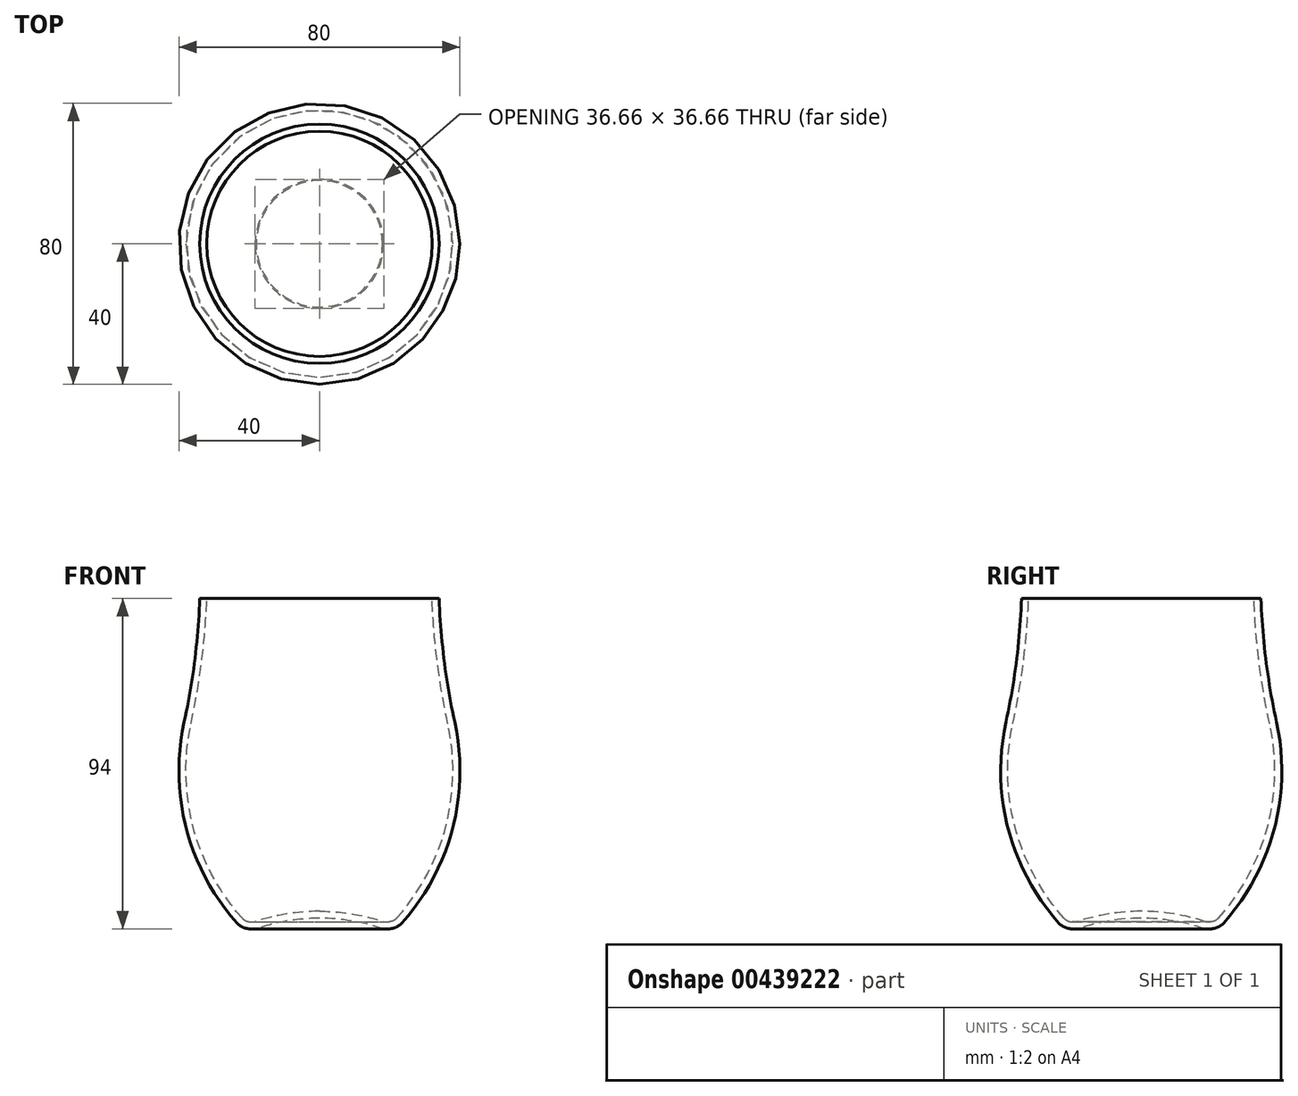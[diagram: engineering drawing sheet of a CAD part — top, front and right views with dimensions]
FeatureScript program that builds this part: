
annotation { "Feature Type Name" : "Feature", "Feature Type Description" : "" }
export const myFeature = defineFeature(function(context is Context, id is Id, definition is map)
    precondition{}
    {
        {
            var Q0;
            Q0=qCreatedBy(makeId("Front.planeOp"),FACE);
            var sketch = newSketch(context, id + "F0", { "sketchPlane" : qUnion([Q0])});
            skLineSegment(sketch, "E0", {"start": v(-18.56, -28.5) * mm, "end": v(-3.7, -28.5) * mm});
            skArc(sketch, "E1", {"start": v(-31.05, -3.22) * mm, "mid": v(-28.63, -15.59) * mm, "end": v(-22.48, -26.6) * mm});
            skLineSegment(sketch, "E2", {"start": v(-31.05, -3.22) * mm, "end": v(-33.2, 58.5) * mm});
            skLineSegment(sketch, "E3", {"start": v(-1.98, -33.5) * mm, "end": v(-2.72, -29.32) * mm});
            skArc(sketch, "E4", {"start": v(-2.72, -29.32) * mm, "mid": v(-3.06, -28.73) * mm, "end": v(-3.7, -28.5) * mm});
            skArc(sketch, "E5", {"start": v(-22.48, -26.6) * mm, "mid": v(-20.74, -28) * mm, "end": v(-18.56, -28.5) * mm});
            skLineSegment(sketch, "E6", {"start": v(0.02, -33.5) * mm, "end": v(-1.98, -33.5) * mm});
            skLineSegment(sketch, "E7", {"start": v(-32.04, 60) * mm, "end": v(-32.68, 60) * mm});
            skLineSegment(sketch, "E8", {"start": v(-32.04, 60) * mm, "end": v(0, 60) * mm});
            skArc(sketch, "E9", {"start": v(-33.15, 58.66) * mm, "mid": v(-33.18, 58.58) * mm, "end": v(-33.2, 58.5) * mm});
            skArc(sketch, "E10", {"start": v(-32.68, 60) * mm, "mid": v(-33.39, 59.5) * mm, "end": v(-33.15, 58.66) * mm});
            skArc(sketch, "E11", {"start": v(-21.95, -21.82) * mm, "mid": v(-20.14, -23.5) * mm, "end": v(-17.75, -24.1) * mm});
            skArc(sketch, "E12", {"start": v(-30.8, 59.43) * mm, "mid": v(-30.98, 59.84) * mm, "end": v(-31.4, 60) * mm});
            skLineSegment(sketch, "E13", {"start": v(-32.04, 60) * mm, "end": v(-31.4, 60) * mm});
            skLineSegment(sketch, "E14", {"start": v(-27.82, -3.55) * mm, "end": v(-30.8, 59.43) * mm});
            skArc(sketch, "E15", {"start": v(-27.82, -3.55) * mm, "mid": v(-26.1, -13.07) * mm, "end": v(-21.95, -21.82) * mm});
            skArc(sketch, "E16", {"start": v(-3.12, -47.12) * mm, "mid": v(-1.62, -47.77) * mm, "end": v(0, -48) * mm});
            skArc(sketch, "E17", {"start": v(-3.12, -47.12) * mm, "mid": v(-9.17, -48.1) * mm, "end": v(-15, -50) * mm});
            skArc(sketch, "E18", {"start": v(0, -45) * mm, "mid": v(-7.84, -45.75) * mm, "end": v(-15.4, -48) * mm});
            skArc(sketch, "E19", {"start": v(-33.63, 59.25) * mm, "mid": v(-33.5, 58.86) * mm, "end": v(-33.13, 58.66) * mm});
            skArc(sketch, "E20", {"start": v(-32.88, 60) * mm, "mid": v(-33.41, 59.78) * mm, "end": v(-33.63, 59.25) * mm});
            skArc(sketch, "E21", {"start": v(-34, 36.18) * mm, "mid": v(-33.25, 47.4) * mm, "end": v(-33.13, 58.66) * mm});
            skLineSegment(sketch, "E22", {"start": v(-21.19, -50) * mm, "end": v(0, -50) * mm});
            skArc(sketch, "E23", {"start": v(-40.33, 5.1) * mm, "mid": v(-40.55, -24.39) * mm, "end": v(-24.12, -48.89) * mm});
            skArc(sketch, "E24", {"start": v(-24.12, -48.89) * mm, "mid": v(-22.64, -49.72) * mm, "end": v(-20.97, -50) * mm});
            skArc(sketch, "E25", {"start": v(-40.33, 5.1) * mm, "mid": v(-36.34, 20.47) * mm, "end": v(-34, 36.18) * mm});
            skArc(sketch, "E26", {"start": v(-32.01, 35.99) * mm, "mid": v(-31.24, 47.69) * mm, "end": v(-31.15, 59.41) * mm});
            skArc(sketch, "E27", {"start": v(-38.42, 4.5) * mm, "mid": v(-34.38, 20.08) * mm, "end": v(-32.01, 35.99) * mm});
            skArc(sketch, "E28", {"start": v(-38.42, 4.5) * mm, "mid": v(-38.64, -23.81) * mm, "end": v(-22.86, -47.33) * mm});
            skArc(sketch, "E29", {"start": v(-22.86, -47.33) * mm, "mid": v(-21.98, -47.83) * mm, "end": v(-20.97, -48) * mm});
            skLineSegment(sketch, "E30", {"start": v(-21.14, -48) * mm, "end": v(-15.4, -48) * mm});
            skArc(sketch, "E31", {"start": v(-31.15, 59.41) * mm, "mid": v(-31.33, 59.83) * mm, "end": v(-31.75, 60) * mm});
            skLineSegment(sketch, "E32", {"start": v(-32.88, 60) * mm, "end": v(-31.75, 60) * mm});
            skLineSegment(sketch, "E33", {"start": v(-28.41, 60) * mm, "end": v(0, 60) * mm});
            skLineSegment(sketch, "E34", {"start": v(-17.75, -24.1) * mm, "end": v(0, -24.1) * mm});
            skLineSegment(sketch, "E35", {"start": v(18.56, -28.5) * mm, "end": v(3.7, -28.5) * mm});
            skArc(sketch, "E36", {"start": v(22.48, -26.6) * mm, "mid": v(28.63, -15.59) * mm, "end": v(31.05, -3.22) * mm});
            skLineSegment(sketch, "E37", {"start": v(31.05, -3.22) * mm, "end": v(33.2, 58.5) * mm});
            skLineSegment(sketch, "E38", {"start": v(1.98, -33.5) * mm, "end": v(2.72, -29.32) * mm});
            skArc(sketch, "E39", {"start": v(3.7, -28.5) * mm, "mid": v(3.06, -28.73) * mm, "end": v(2.72, -29.32) * mm});
            skArc(sketch, "E40", {"start": v(18.56, -28.5) * mm, "mid": v(20.74, -28) * mm, "end": v(22.48, -26.6) * mm});
            skLineSegment(sketch, "E41", {"start": v(-0.02, -33.5) * mm, "end": v(1.98, -33.5) * mm});
            skLineSegment(sketch, "E42", {"start": v(32.04, 60) * mm, "end": v(32.68, 60) * mm});
            skLineSegment(sketch, "E43", {"start": v(32.04, 60) * mm, "end": v(0, 60) * mm});
            skArc(sketch, "E44", {"start": v(33.2, 58.5) * mm, "mid": v(33.18, 58.58) * mm, "end": v(33.15, 58.66) * mm});
            skArc(sketch, "E45", {"start": v(33.15, 58.66) * mm, "mid": v(33.39, 59.5) * mm, "end": v(32.68, 60) * mm});
            skArc(sketch, "E46", {"start": v(17.75, -24.1) * mm, "mid": v(20.14, -23.5) * mm, "end": v(21.95, -21.82) * mm});
            skArc(sketch, "E47", {"start": v(31.4, 60) * mm, "mid": v(30.98, 59.84) * mm, "end": v(30.8, 59.43) * mm});
            skLineSegment(sketch, "E48", {"start": v(32.04, 60) * mm, "end": v(31.4, 60) * mm});
            skLineSegment(sketch, "E49", {"start": v(27.82, -3.55) * mm, "end": v(30.8, 59.43) * mm});
            skArc(sketch, "E50", {"start": v(21.95, -21.82) * mm, "mid": v(26.1, -13.07) * mm, "end": v(27.82, -3.55) * mm});
            skArc(sketch, "E51", {"start": v(0, -48) * mm, "mid": v(1.62, -47.77) * mm, "end": v(3.12, -47.12) * mm});
            skArc(sketch, "E52", {"start": v(15, -50) * mm, "mid": v(9.17, -48.1) * mm, "end": v(3.12, -47.12) * mm});
            skArc(sketch, "E53", {"start": v(15.4, -48) * mm, "mid": v(7.84, -45.75) * mm, "end": v(0, -45) * mm});
            skArc(sketch, "E54", {"start": v(33.13, 58.66) * mm, "mid": v(33.5, 58.86) * mm, "end": v(33.63, 59.25) * mm});
            skArc(sketch, "E55", {"start": v(33.63, 59.25) * mm, "mid": v(33.41, 59.78) * mm, "end": v(32.88, 60) * mm});
            skArc(sketch, "E56", {"start": v(33.13, 58.66) * mm, "mid": v(33.25, 47.4) * mm, "end": v(34, 36.18) * mm});
            skLineSegment(sketch, "E57", {"start": v(21.19, -50) * mm, "end": v(0, -50) * mm});
            skArc(sketch, "E58", {"start": v(24.12, -48.89) * mm, "mid": v(40.55, -24.39) * mm, "end": v(40.33, 5.1) * mm});
            skArc(sketch, "E59", {"start": v(20.97, -50) * mm, "mid": v(22.64, -49.72) * mm, "end": v(24.12, -48.89) * mm});
            skArc(sketch, "E60", {"start": v(34, 36.18) * mm, "mid": v(36.34, 20.47) * mm, "end": v(40.33, 5.1) * mm});
            skArc(sketch, "E61", {"start": v(31.15, 59.41) * mm, "mid": v(31.24, 47.69) * mm, "end": v(32.01, 35.99) * mm});
            skArc(sketch, "E62", {"start": v(32.01, 35.99) * mm, "mid": v(34.38, 20.08) * mm, "end": v(38.42, 4.5) * mm});
            skArc(sketch, "E63", {"start": v(22.86, -47.33) * mm, "mid": v(38.64, -23.81) * mm, "end": v(38.42, 4.5) * mm});
            skArc(sketch, "E64", {"start": v(20.97, -48) * mm, "mid": v(21.98, -47.83) * mm, "end": v(22.86, -47.33) * mm});
            skLineSegment(sketch, "E65", {"start": v(21.14, -48) * mm, "end": v(15.4, -48) * mm});
            skArc(sketch, "E66", {"start": v(31.75, 60) * mm, "mid": v(31.33, 59.83) * mm, "end": v(31.15, 59.41) * mm});
            skLineSegment(sketch, "E67", {"start": v(32.88, 60) * mm, "end": v(31.75, 60) * mm});
            skLineSegment(sketch, "E68", {"start": v(28.41, 60) * mm, "end": v(0, 60) * mm});
            skLineSegment(sketch, "E69", {"start": v(17.75, -24.1) * mm, "end": v(0, -24.1) * mm});
            skArc(sketch, "E70", {"start": v(-40.4, 1.6) * mm, "mid": v(-40.69, -30.54) * mm, "end": v(-24.85, -58.5) * mm});
            skArc(sketch, "E71", {"start": v(-24.85, -58.5) * mm, "mid": v(-23.22, -59.61) * mm, "end": v(-21.29, -60) * mm});
            skArc(sketch, "E72", {"start": v(-38.47, 1.07) * mm, "mid": v(-32.68, 29.97) * mm, "end": v(-31.15, 59.41) * mm});
            skArc(sketch, "E73", {"start": v(-38.47, 1.07) * mm, "mid": v(-38.75, -30.04) * mm, "end": v(-23.43, -57.1) * mm});
            skArc(sketch, "E74", {"start": v(-23.43, -57.1) * mm, "mid": v(-22.45, -57.77) * mm, "end": v(-21.29, -58) * mm});
            skArc(sketch, "E75", {"start": v(-40.4, 1.6) * mm, "mid": v(-34.7, 29.87) * mm, "end": v(-33.13, 58.66) * mm});
            skLineSegment(sketch, "E76", {"start": v(-31.75, 60) * mm, "end": v(-3.33, 60) * mm});
            skLineSegment(sketch, "E77", {"start": v(-21.29, -60) * mm, "end": v(0, -60) * mm});
            skArc(sketch, "E78", {"start": v(-3.12, -57.13) * mm, "mid": v(-1.62, -57.78) * mm, "end": v(0, -58) * mm});
            skArc(sketch, "E79", {"start": v(-3.12, -57.13) * mm, "mid": v(-9.17, -58.1) * mm, "end": v(-15, -60) * mm});
            skArc(sketch, "E80", {"start": v(0, -55) * mm, "mid": v(-7.84, -55.76) * mm, "end": v(-15.4, -58) * mm});
            skLineSegment(sketch, "E81", {"start": v(-21.29, -58) * mm, "end": v(-15.4, -58) * mm});
            skArc(sketch, "E82", {"start": v(25, -58.4) * mm, "mid": v(40.71, -30.36) * mm, "end": v(40.3, 1.78) * mm});
            skArc(sketch, "E83", {"start": v(21.44, -59.91) * mm, "mid": v(23.37, -59.51) * mm, "end": v(25, -58.4) * mm});
            skArc(sketch, "E84", {"start": v(23.57, -57) * mm, "mid": v(38.78, -29.87) * mm, "end": v(38.37, 1.23) * mm});
            skArc(sketch, "E85", {"start": v(21.43, -57.91) * mm, "mid": v(22.6, -57.67) * mm, "end": v(23.57, -57) * mm});
            skLineSegment(sketch, "E86", {"start": v(21.44, -59.91) * mm, "end": v(0.15, -60) * mm});
            skArc(sketch, "E87", {"start": v(0.14, -58) * mm, "mid": v(1.76, -57.77) * mm, "end": v(3.26, -57.11) * mm});
            skArc(sketch, "E88", {"start": v(15.15, -59.94) * mm, "mid": v(9.32, -58.06) * mm, "end": v(3.26, -57.11) * mm});
            skArc(sketch, "E89", {"start": v(15.54, -57.94) * mm, "mid": v(7.98, -55.73) * mm, "end": v(0.13, -55) * mm});
            skLineSegment(sketch, "E90", {"start": v(21.43, -57.91) * mm, "end": v(15.54, -57.94) * mm});
            skArc(sketch, "E91", {"start": v(32.78, 58.8) * mm, "mid": v(34.48, 30.01) * mm, "end": v(40.3, 1.78) * mm});
            skArc(sketch, "E92", {"start": v(30.8, 59.54) * mm, "mid": v(32.45, 30.11) * mm, "end": v(38.37, 1.23) * mm});
            skSolve(sketch);
        }
        {
            var Q0;
            Q0=qCreatedBy(makeId("Front.planeOp"),FACE);
            var sketch = newSketch(context, id + "F1", { "sketchPlane" : qUnion([Q0])});
            skArc(sketch, "E93.0", {"start": v(-32.88, 60) * mm, "mid": v(-33.41, 59.78) * mm, "end": v(-33.63, 59.25) * mm});
            skArc(sketch, "E94.0", {"start": v(-33.63, 59.25) * mm, "mid": v(-33.5, 58.87) * mm, "end": v(-33.15, 58.66) * mm});
            skArc(sketch, "E95.0", {"start": v(-33.15, 58.66) * mm, "mid": v(-33.18, 58.58) * mm, "end": v(-33.2, 58.5) * mm});
            skPoint(sketch, "E96.orphan", {"position": v(-33.15, 58.66) * mm});
            skPoint(sketch, "E97.orphan", {"position": v(-33.13, 58.66) * mm});
            skSolve(sketch);
        }
        {
            var Q0;
            Q0=qCreatedBy(makeId("Front.planeOp"),FACE);
            var sketch = newSketch(context, id + "F2", { "sketchPlane" : qUnion([Q0])});
            skArc(sketch, "E98.0", {"start": v(-32.88, 60) * mm, "mid": v(-33.41, 59.78) * mm, "end": v(-33.63, 59.25) * mm});
            skArc(sketch, "E99.0", {"start": v(-33.63, 59.25) * mm, "mid": v(-33.5, 58.87) * mm, "end": v(-33.15, 58.66) * mm});
            skArc(sketch, "E100.0", {"start": v(-33.15, 58.66) * mm, "mid": v(-33.18, 58.58) * mm, "end": v(-33.2, 58.5) * mm});
            skLineSegment(sketch, "E101", {"start": v(-33.2, 58.5) * mm, "end": v(-34.05, 34.42) * mm});
            skArc(sketch, "E102", {"start": v(-38.51, -1.17) * mm, "mid": v(-37.56, -32.66) * mm, "end": v(-21.9, -60) * mm});
            skLineSegment(sketch, "E103", {"start": v(-21.9, -60) * mm, "end": v(0, -60) * mm, "construction": true});
            skPoint(sketch, "E104.visualSharp", {"position": v(-34.9, 10.25) * mm});
            skArc(sketch, "E104.filletArc", {"start": v(-38.51, -1.17) * mm, "mid": v(-35.48, 16.53) * mm, "end": v(-34.05, 34.42) * mm});
            skArc(sketch, "E105", {"start": v(0, -57) * mm, "mid": v(-9.12, -57.76) * mm, "end": v(-18, -60) * mm});
            skArc(sketch, "E106.0", {"start": v(-36.56, -1.6) * mm, "mid": v(-33.5, 16.28) * mm, "end": v(-32.05, 34.35) * mm});
            skArc(sketch, "E107.0", {"start": v(-36.56, -1.6) * mm, "mid": v(-35.74, -31.7) * mm, "end": v(-21.04, -58) * mm});
            skArc(sketch, "E108.0", {"start": v(0, -55) * mm, "mid": v(-9.29, -55.76) * mm, "end": v(-18.33, -58) * mm});
            skLineSegment(sketch, "E109", {"start": v(-18.33, -58) * mm, "end": v(-21.04, -58) * mm});
            skLineSegment(sketch, "E110.0", {"start": v(-31.16, 60) * mm, "end": v(-32.05, 34.35) * mm});
            skLineSegment(sketch, "E111", {"start": v(-32.88, 60) * mm, "end": v(-31.16, 60) * mm});
            skLineSegment(sketch, "E112", {"start": v(-21.9, -60) * mm, "end": v(-18, -60) * mm});
            skLineSegment(sketch, "E113", {"start": v(0, -57) * mm, "end": v(0, -55) * mm});
            skLineSegment(sketch, "E114", {"start": v(0, -112.5) * mm, "end": v(0, -57) * mm, "construction": true});
            skLineSegment(sketch, "E115", {"start": v(0, -55) * mm, "end": v(0, 0) * mm, "construction": true});
            skPoint(sketch, "E116.orphan", {"position": v(-32.95, 8.7) * mm});
            skSolve(sketch);
        }
        {
            var Q0;
            Q0 = qSketchRegion(id + "F2", true);
            var Q1;
            Q1=sQuery(id+"F2.wireOp",EDGE,"E113");
            revolve(context, id + "F3", {"entities" : qUnion([Q0]), "axis" : qUnion([Q1]), "revolveType" : RevolveType.FULL});
        }
        {
            var Q0;
            Q0=makeQuery(id+"F3.opRevolve","SWEPT_EDGE",EDGE,{"disambiguationData":[OSD([sQuery(id+"F2.wireOp",EDGE,"E102"),sQuery(id+"F2.wireOp",EDGE,"E112")])]});
            fillet(context, id + "F4", {"entities" : qUnion([Q0]), "radius" : 5 * mm, "tangentPropagation" : true, "allowEdgeOverflow" : false});
        }
        {
            var Q0;
            Q0=makeQuery(id+"F3.opRevolve","SWEPT_EDGE",EDGE,{"disambiguationData":[OSD([sQuery(id+"F2.wireOp",EDGE,"E107.0"),sQuery(id+"F2.wireOp",EDGE,"E109")])]});
            fillet(context, id + "F5", {"entities" : qUnion([Q0]), "radius" : 3 * mm, "tangentPropagation" : true, "allowEdgeOverflow" : false});
        }
        {
            var Q0;
            Q0=makeQuery(id+"F3.opRevolve","SWEPT_EDGE",EDGE,{"disambiguationData":[OSD([sQuery(id+"F2.wireOp",EDGE,"E110.0"),sQuery(id+"F2.wireOp",EDGE,"E111")])]});
            fillet(context, id + "F6", {"entities" : qUnion([Q0]), "radius" : .6 * mm, "tangentPropagation" : true, "allowEdgeOverflow" : false});
        }
        {
            var Q0;
            Q0=qCreatedBy(makeId("Front.planeOp"),FACE);
            var sketch = newSketch(context, id + "F7", { "sketchPlane" : qUnion([Q0])});
            skLineSegment(sketch, "E117.0", {"start": v(-31.18, 59.38) * mm, "end": v(-32.05, 34.35) * mm});
            skArc(sketch, "E118.0", {"start": v(-36.56, -1.6) * mm, "mid": v(-33.5, 16.28) * mm, "end": v(-32.05, 34.35) * mm});
            skArc(sketch, "E119.0", {"start": v(-36.56, -1.6) * mm, "mid": v(-35.74, -31.7) * mm, "end": v(-21.04, -58) * mm});
            skLineSegment(sketch, "E120.0", {"start": v(-18.33, -58) * mm, "end": v(-21.04, -58) * mm});
            skArc(sketch, "E121.0", {"start": v(0, -55) * mm, "mid": v(-9.29, -55.76) * mm, "end": v(-18.33, -58) * mm});
            skPoint(sketch, "E122.visualSharp", {"position": v(-31.16, 60) * mm});
            skArc(sketch, "E122.filletArc", {"start": v(-31.18, 59.38) * mm, "mid": v(-31.34, 59.81) * mm, "end": v(-31.78, 60) * mm});
            skPoint(sketch, "E123.0.start.orphan", {"position": v(-32.88, 60) * mm});
            skLineSegment(sketch, "E124", {"start": v(-31.78, 60) * mm, "end": v(0, 60) * mm});
            skLineSegment(sketch, "E125", {"start": v(0, -55) * mm, "end": v(0, 60) * mm});
            skSolve(sketch);
        }
        {
            var Q0;
            Q0 = qSketchRegion(id + "F7", true);
            var Q1;
            Q1=sQuery(id+"F7.wireOp",EDGE,"E125");
            revolve(context, id + "F8", {"entities" : qUnion([Q0]), "axis" : qUnion([Q1]), "revolveType" : RevolveType.FULL});
        }
        {
            var Q0;
            Q0=makeQuery(id+"F8.opRevolve","SWEPT_EDGE",EDGE,{"disambiguationData":[OSD([sQuery(id+"F7.wireOp",EDGE,"E119.0"),sQuery(id+"F7.wireOp",EDGE,"E120.0")])]});
            fillet(context, id + "F9", {"entities" : qUnion([Q0]), "radius" : 3 * mm, "tangentPropagation" : true, "allowEdgeOverflow" : false});
        }
        {
            var Q0;
            Q0=makeQuery(id+"F8.opRevolve","SWEPT_FACE",FACE,{"disambiguationData":[OSD([sQuery(id+"F7.wireOp",EDGE,"E124")])]});
            var sketch = newSketch(context, id + "F10", { "sketchPlane" : qUnion([Q0])});
            skCircle(sketch, "E126", {"center": v(0, 0) * mm, "radius": 90.6 * mm});
            skSolve(sketch);
        }
        {
            var Q0;
            Q0 = qSketchRegion(id + "F10", true);
            extrude(context, id + "F11", {"entities" : qUnion([Q0]), "operationType" : NewBodyOperationType.REMOVE, "oppositeDirection" : true, "depth" : 26 * mm});
        }
    });
